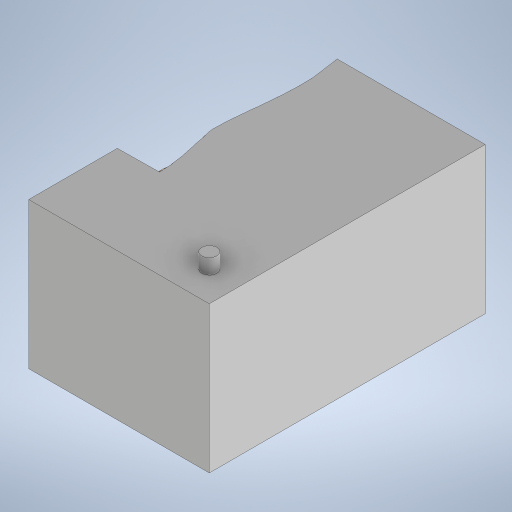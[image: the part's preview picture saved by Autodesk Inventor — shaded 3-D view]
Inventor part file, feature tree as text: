
AUTODESK INVENTOR PART (.ipt)
format: ipt  version: 2024 (Build 280153000, 153)  size: 10,744,320 bytes
history: native  units: mm
features: other x6, extrude x6, sketch x6, plane x2
ambient origin geometry x8: Origin, YZ Plane, XZ Plane, XY Plane, X Axis, Y Axis, Z Axis, Center Point
bodies: Body1 (feature_tree)
feature tree (20):
  other  "M.ipt"
  plane  "Plano de trabajo1"
  extrude  "Extrusión1"  [1 undecoded]
  other  "Combinar1"
  sketch  "Boceto3"  dims[d2=550.0mm d3=520.0mm]
  sketch  "Boceto4"  dims[d4=550.0mm d5=0.0mm d6=129.8482mm]
  plane  "Plano de trabajo2"
  sketch  "Boceto5"  dims[d17=180.0mm d18=180.0mm]
  extrude  "Extrusión2"  Depth=520.0mm
  extrude  "Extrusión3"  Depth=129.8482mm
  extrude  "Extrusión4"  Depth=180.0mm
  extrude  "Extrusión5"  Depth=180.0mm
  extrude  "Extrusión6"  Depth=180.0mm
  other  "Sólido1::M.ipt"
  other  "OperaciónIdentificador1"
  sketch  "Boceto1"  dims[d0=25.0mm d1=-365.0mm]
  other  "Sólido2"
  sketch  "Boceto6"  dims[d22=326.0mm d23=180.0mm]
  sketch  "Boceto7"  dims[d24=180.0mm d25=180.0mm d26=10.0mm d27=0.0mm d28=1000.0mm d29=0.0mm d30=1000.0mm d31=0.0mm d32=30.0mm d33=30.0mm d34=16.0mm d35=16.0mm d36=0.0mm d37=30.0mm d38=30.0mm d39=15.0mm d40=15.0mm d41=161.0mm d42=0.0mm d43=0.0mm d14=0.5mm d15=0.872665mm d16=0.5mm d19=0.5mm d20=0.872665mm d21=0.5mm]
  other  "Sólido1"
note: 1 required parameter value undecoded (feature->parameter linkage not recoverable at this tier; creation-order binding heuristic only, values carry confidence <= 0.55)
